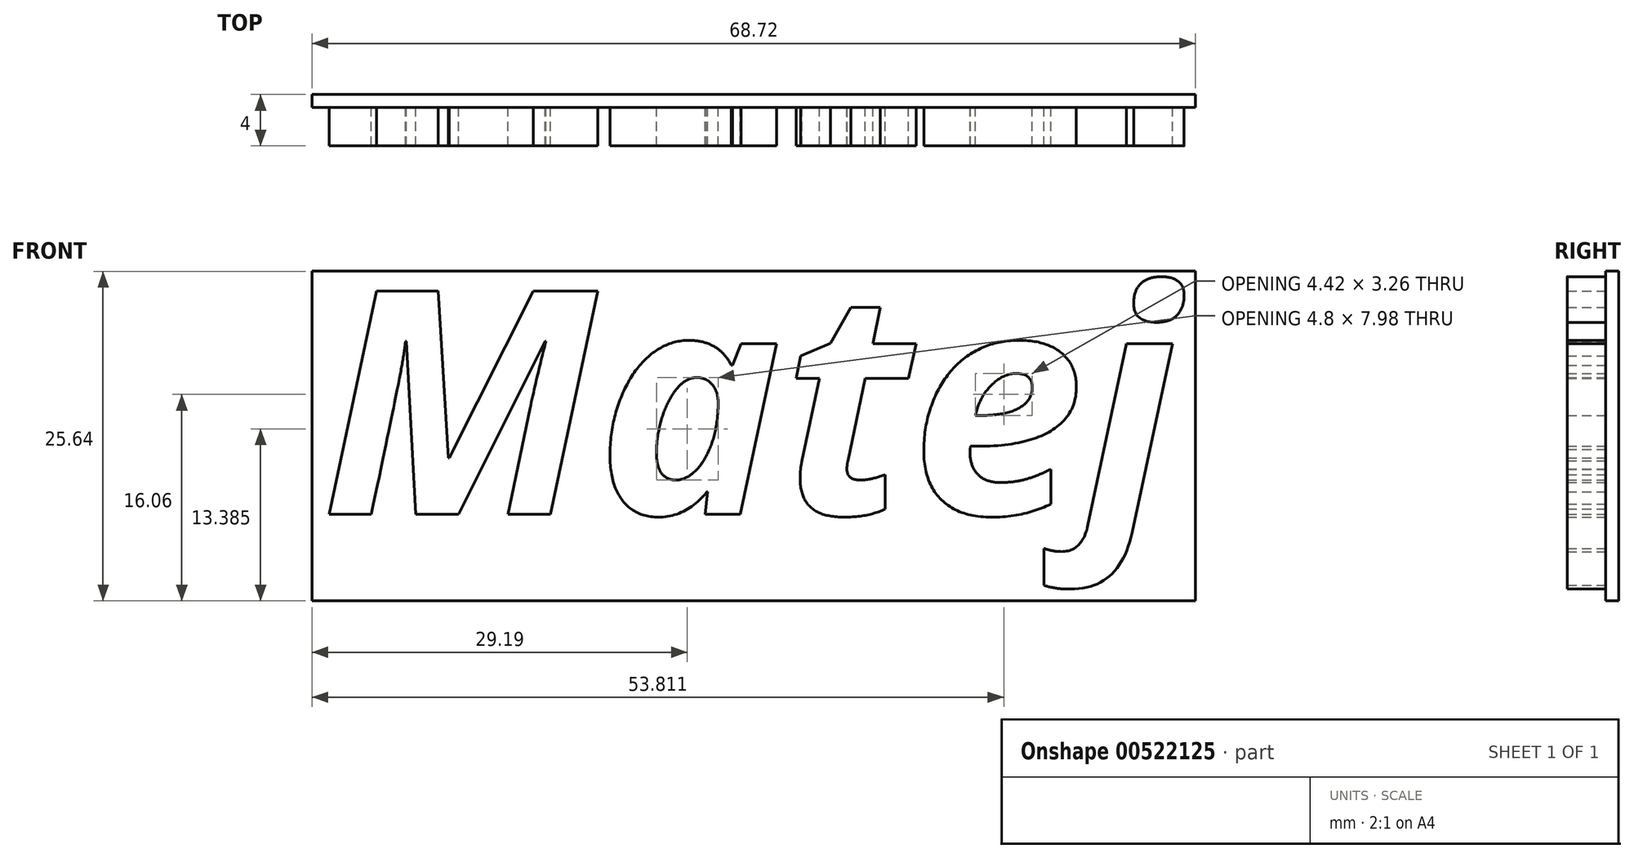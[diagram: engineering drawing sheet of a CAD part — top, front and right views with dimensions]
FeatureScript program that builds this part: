
annotation { "Feature Type Name" : "Feature", "Feature Type Description" : "" }
export const myFeature = defineFeature(function(context is Context, id is Id, definition is map)
    precondition{}
    {
        {
            var Q0;
            Q0=qCreatedBy(makeId("Front.planeOp"),FACE);
            var sketch = newSketch(context, id + "F0", { "sketchPlane" : qUnion([Q0])});
            skText(sketch, "E0", { "text": "Matej", "fontName": "OpenSans-BoldItalic.ttf"});
            const initialGuessF0  = {"E0": [-0.04475, -0.00012, 1, 0, 0.0175]};
            skSetInitialGuess(sketch, initialGuessF0);
            skSolve(sketch);
        }
        {
            var Q0;
            Q0=qSketchRegion(id+"F0",true);
            extrude(context, id + "F1", {"entities" : qUnion([Q0]), "depth" : 3 * mm});
        }
        {
            var Q0;
            Q0=makeQuery(id+"F0.imprint","IMPRINT",FACE,{"disambiguationData":[TD([[makeQuery(id+"F0.imprint","IMPRINT",EDGE,{"derivedFrom":sQuery(id+"F0.wireOp",EDGE,"E0.sketch_text.stroke-36")}),-1.0]])]});
            var sketch = newSketch(context, id + "F2", { "sketchPlane" : qUnion([Q0])});
            skLineSegment(sketch, "E1.bottom", {"start": v(-45.47, 18.77) * mm, "end": v(23.25, 18.77) * mm});
            skLineSegment(sketch, "E1.top", {"start": v(-45.47, -6.87) * mm, "end": v(23.25, -6.87) * mm});
            skLineSegment(sketch, "E1.left", {"start": v(-45.47, 18.77) * mm, "end": v(-45.47, -6.87) * mm});
            skLineSegment(sketch, "E1.right", {"start": v(23.25, 18.77) * mm, "end": v(23.25, -6.87) * mm});
            skSolve(sketch);
        }
        {
            var Q0;
            Q0=qSketchRegion(id+"F2",true);
            extrude(context, id + "F3", {"entities" : qUnion([Q0]), "oppositeDirection" : true, "depth" : 1 * mm, "offsetDistance" : 25 * mm});
        }
    });
